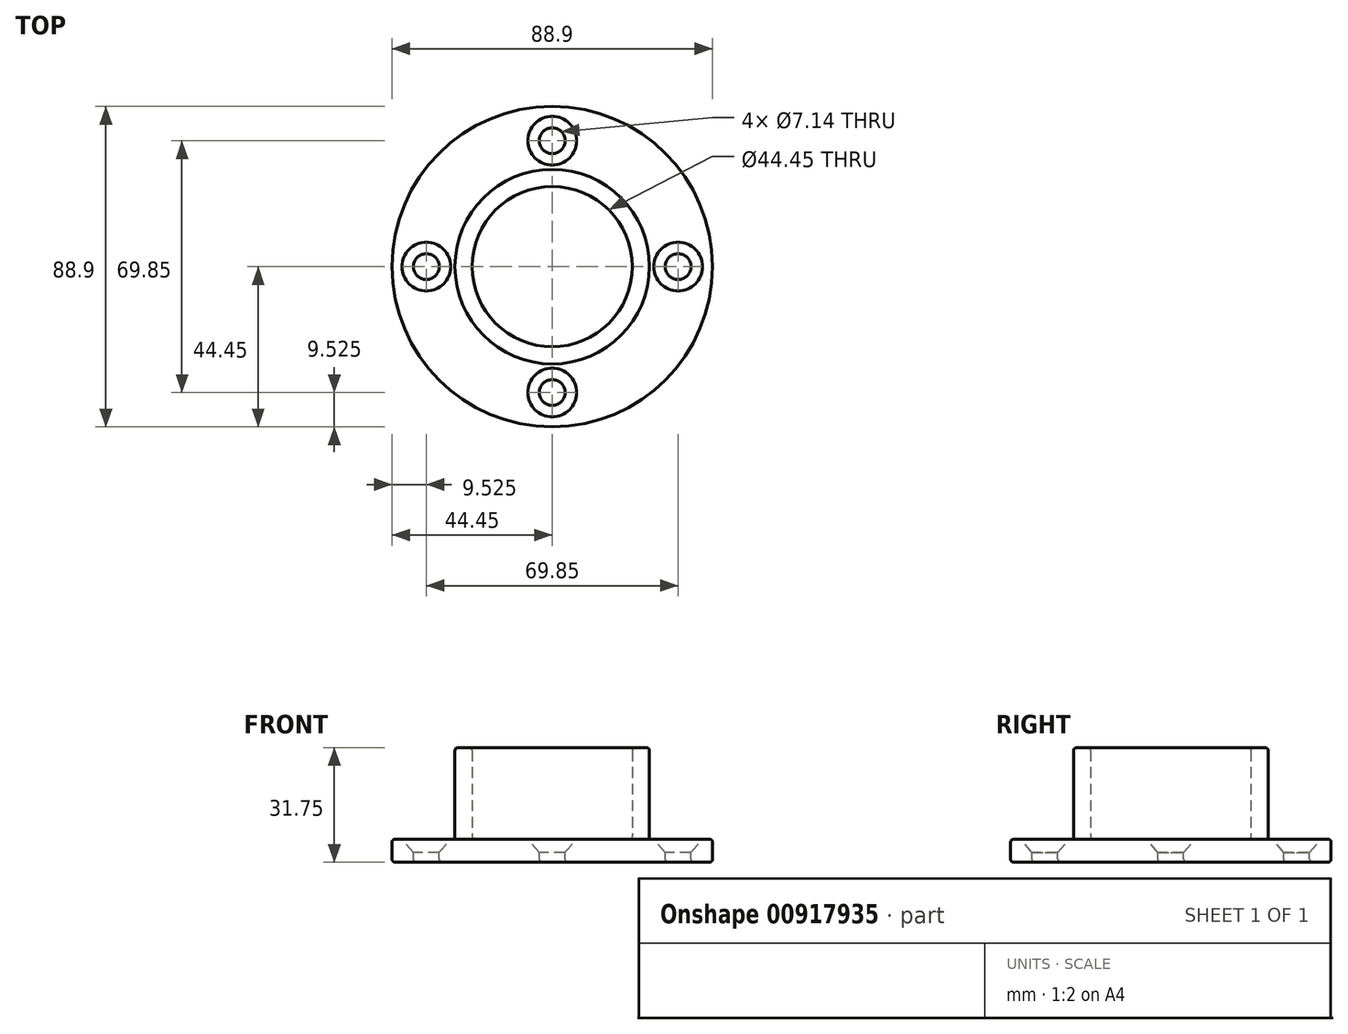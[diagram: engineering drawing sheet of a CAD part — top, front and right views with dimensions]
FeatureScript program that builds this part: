
annotation { "Feature Type Name" : "Feature", "Feature Type Description" : "" }
export const myFeature = defineFeature(function(context is Context, id is Id, definition is map)
    precondition{}
    {
        {
            var Q0;
            Q0=qCreatedBy(makeId("Top.planeOp"),FACE);
            var sketch = newSketch(context, id + "F0", { "sketchPlane" : qUnion([Q0])});
            skCircle(sketch, "E0", {"center": v(0, 0) * mm, "radius": 44.45 * mm});
            skCircle(sketch, "E1", {"center": v(0, 0) * mm, "radius": 22.23 * mm});
            skCircle(sketch, "E2", {"center": v(0, 0) * mm, "radius": 26.99 * mm});
            skSolve(sketch);
        }
        {
            var Q0;
            Q0=makeQuery(id+"F0.imprint","IMPRINT",FACE,{"disambiguationData":[TD([[makeQuery(id+"F0.imprint","IMPRINT",EDGE,{"derivedFrom":sQuery(id+"F0.wireOp",EDGE,"E1")}),-1.0]])]});
            extrude(context, id + "F1", {"entities" : qUnion([Q0]), "depth" : 25.4 * mm, "offsetDistance" : 25.4 * mm});
        }
        {
            var Q0;
            Q0=makeQuery(id+"F0.imprint","IMPRINT",FACE,{"disambiguationData":[TD([[makeQuery(id+"F0.imprint","IMPRINT",EDGE,{"derivedFrom":sQuery(id+"F0.wireOp",EDGE,"E1")}),1.0]])]});
            var Q1;
            Q1=makeQuery(id+"F0.imprint","IMPRINT",FACE,{"disambiguationData":[TD([[makeQuery(id+"F0.imprint","IMPRINT",EDGE,{"derivedFrom":sQuery(id+"F0.wireOp",EDGE,"E1")}),-1.0]])]});
            var Q2;
            Q2=makeQuery(id+"F0.imprint","IMPRINT",FACE,{"disambiguationData":[TD([[makeQuery(id+"F0.imprint","IMPRINT",EDGE,{"derivedFrom":sQuery(id+"F0.wireOp",EDGE,"E0")}),1.0]])]});
            var Q3;
            Q3=makeQuery(id+"F1.opExtrude","CAP_FACE",FACE,{"disambiguationData":[OSD([sQuery(id+"F0.wireOp",EDGE,"E1"),sQuery(id+"F0.wireOp",EDGE,"E2")])],"isStart":true});
            var Q4;
            Q4=sQuery(id+"F0.wireOp",EDGE,"E0");
            extrude(context, id + "F2", {"entities" : qUnion([Q0, Q1, Q2, Q3]), "operationType" : NewBodyOperationType.ADD, "surfaceEntities" : qUnion([Q4]), "oppositeDirection" : true, "depth" : 6.35 * mm, "offsetDistance" : 25.4 * mm});
        }
        {
            var Q0;
            Q0=qCreatedBy(makeId("Top.planeOp"),FACE);
            var sketch = newSketch(context, id + "F3", { "sketchPlane" : qUnion([Q0])});
            skPoint(sketch, "E3", {"position": v(0, -34.93) * mm});
            skPoint(sketch, "E4", {"position": v(34.93, 0) * mm});
            skPoint(sketch, "E5", {"position": v(-34.93, 0) * mm});
            skPoint(sketch, "E6", {"position": v(0, 34.93) * mm});
            skSolve(sketch);
        }
        {
            var Q0;
            Q0=sQuery(id+"F3.wireOp",VERTEX,"E5");
            var Q1;
            Q1=sQuery(id+"F3.wireOp",VERTEX,"E6");
            var Q2;
            Q2=sQuery(id+"F3.wireOp",VERTEX,"E4");
            var Q3;
            Q3=sQuery(id+"F3.wireOp",VERTEX,"E3");
            var Q4;
            Q4=makeQuery(id+"F1.opExtrude","SWEPT_BODY",BODY,{"disambiguationData":[OSD([sQuery(id+"F0.wireOp",EDGE,"E1"),sQuery(id+"F0.wireOp",EDGE,"E2")])]});
            hole(context, id + "F4", {"style" : HoleStyle.C_SINK, "endStyle" : HoleEndStyle.THROUGH, "standardTappedOrClearance" : lookupTablePath({ "fit" : "Normal (ASME)", "standard" : "ANSI", "size" : "1/4", "type" : "Clearance" }), "standardBlindInLast" : lookupTablePath({ "fit" : "Normal", "standard" : "ANSI", "size" : "1/4", "type" : "Clearance" }), "holeDiameter" : 7.14 * mm, "cSinkDiameter" : 13.5 * mm, "cSinkAngle" : 82 * degree, "majorDiameter" : 6.35 * mm, "isTappedThrough" : true, "tappedDepth" : 12.7 * mm, "tapClearance" : 3, "startFromSketch" : true, "locations" : qUnion([Q0, Q1, Q2, Q3]), "scope" : qUnion([Q4])});
        }
        {
            var Q0;
            Q0=makeQuery(id+"F1.opExtrude","CAP_EDGE",EDGE,{"disambiguationData":[OSD([sQuery(id+"F0.wireOp",EDGE,"E2")])],"isStart":false});
            var Q1;
            Q1=makeQuery(id+"F2.opExtrude","CAP_EDGE",EDGE,{"disambiguationData":[OSD([sQuery(id+"F0.wireOp",EDGE,"E0")])],"isStart":true});
            var Q2;
            Q2=makeQuery(id+"F2.opExtrude","CAP_EDGE",EDGE,{"disambiguationData":[OSD([sQuery(id+"F0.wireOp",EDGE,"E0")])],"isStart":false});
            var Q3;
            Q3=makeQuery(id+"F4.hole-3.boolean.opBoolean","INTERSECT",EDGE,{"derivedFrom":[makeQuery(id+"F2.opExtrude","CAP_FACE",FACE,{"disambiguationData":[OSD([sQuery(id+"F0.wireOp",EDGE,"E0")])],"isStart":false}),makeQuery(id+"F4.hole-3.opRevolve","SWEPT_FACE",FACE,{"disambiguationData":[OSD([sQuery(id+"F4.hole-3.sketch.wireOp",EDGE,"core_line_2")])]})]});
            var Q4;
            Q4=makeQuery(id+"F4.hole-2.boolean.opBoolean","INTERSECT",EDGE,{"derivedFrom":[makeQuery(id+"F2.opExtrude","CAP_FACE",FACE,{"disambiguationData":[OSD([sQuery(id+"F0.wireOp",EDGE,"E0")])],"isStart":false}),makeQuery(id+"F4.hole-2.opRevolve","SWEPT_FACE",FACE,{"disambiguationData":[OSD([sQuery(id+"F4.hole-2.sketch.wireOp",EDGE,"core_line_2")])]})]});
            var Q5;
            Q5=makeQuery(id+"F4.hole-1.boolean.opBoolean","INTERSECT",EDGE,{"derivedFrom":[makeQuery(id+"F2.opExtrude","CAP_FACE",FACE,{"disambiguationData":[OSD([sQuery(id+"F0.wireOp",EDGE,"E0")])],"isStart":false}),makeQuery(id+"F4.hole-1.opRevolve","SWEPT_FACE",FACE,{"disambiguationData":[OSD([sQuery(id+"F4.hole-1.sketch.wireOp",EDGE,"core_line_2")])]})]});
            var Q6;
            Q6=makeQuery(id+"F2.opExtrude","CAP_FACE",FACE,{"disambiguationData":[OSD([sQuery(id+"F0.wireOp",EDGE,"E0")])],"isStart":false});
            var Q7;
            Q7=makeQuery(id+"F1.opExtrude","CAP_EDGE",EDGE,{"disambiguationData":[OSD([sQuery(id+"F0.wireOp",EDGE,"E1")])],"isStart":false});
            var Q8;
            Q8=makeQuery(id+"F1.opExtrude","SWEPT_FACE",FACE,{"disambiguationData":[OSD([sQuery(id+"F0.wireOp",EDGE,"E1")])]});
            fillet(context, id + "F5", {"entities" : qUnion([Q0, Q1, Q2, Q3, Q4, Q5, Q6, Q7, Q8]), "radius" : 0.8 * mm, "tangentPropagation" : true, "allowEdgeOverflow" : false});
        }
    });
